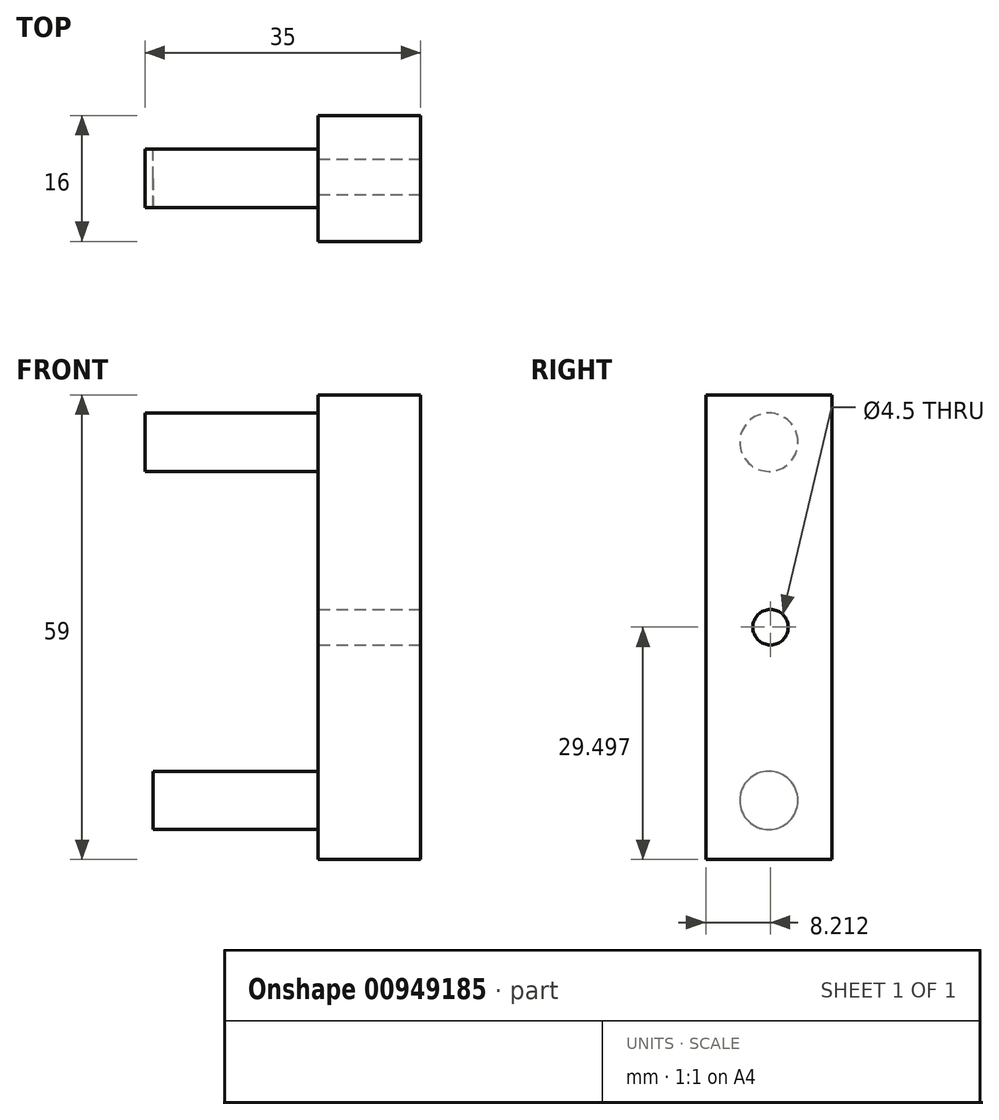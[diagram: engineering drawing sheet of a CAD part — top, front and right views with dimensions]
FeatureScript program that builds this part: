
annotation { "Feature Type Name" : "Feature", "Feature Type Description" : "" }
export const myFeature = defineFeature(function(context is Context, id is Id, definition is map)
    precondition{}
    {
        {
            var Q0;
            Q0=qCreatedBy(makeId("Front.planeOp"),FACE);
            var sketch = newSketch(context, id + "F0", { "sketchPlane" : qUnion([Q0])});
            skLineSegment(sketch, "E0.bottom", {"start": v(-12.8, 32) * mm, "end": v(0.2, 32) * mm});
            skLineSegment(sketch, "E1", {"start": v(-12.8, 32) * mm, "end": v(-12.8, 19.5) * mm});
            skLineSegment(sketch, "E2", {"start": v(-12.8, -8.5) * mm, "end": v(-12.8, -27) * mm});
            skLineSegment(sketch, "E3", {"start": v(0.2, 32) * mm, "end": v(0.2, -27) * mm});
            skLineSegment(sketch, "E4", {"start": v(0.2, -27) * mm, "end": v(-12.8, -27) * mm});
            skLineSegment(sketch, "E5", {"start": v(-12.8, 19.5) * mm, "end": v(-12.8, -8.5) * mm});
            skSolve(sketch);
        }
        {
            var Q0;
            Q0=makeQuery(id+"F0.imprint","IMPRINT",FACE,{"disambiguationData":[TD([[makeQuery(id+"F0.imprint","IMPRINT",EDGE,{"derivedFrom":sQuery(id+"F0.wireOp",EDGE,"E0.bottom")}),-1.0]])]});
            extrude(context, id + "F1", {"entities" : qUnion([Q0]), "depth" : 16 * mm, "offsetDistance" : 25 * mm});
        }
        {
            var Q0;
            Q0=makeQuery(id+"F1.opExtrude","SWEPT_FACE",FACE,{"disambiguationData":[OSD([sQuery(id+"F0.wireOp",EDGE,"E1")])]});
            var sketch = newSketch(context, id + "F2", { "sketchPlane" : qUnion([Q0])});
            skCircle(sketch, "E6", {"center": v(8, 26) * mm, "radius": 3.7 * mm});
            skCircle(sketch, "E7", {"center": v(8, -19.5) * mm, "radius": 3.7 * mm});
            skSolve(sketch);
        }
        {
            var Q0;
            Q0=makeQuery(id+"F2.imprint","IMPRINT",FACE,{"disambiguationData":[TD([[makeQuery(id+"F2.imprint","IMPRINT",EDGE,{"derivedFrom":sQuery(id+"F2.wireOp",EDGE,"E6")}),1.0]])]});
            extrude(context, id + "F3", {"entities" : qUnion([Q0]), "operationType" : NewBodyOperationType.ADD, "depth" : 22 * mm, "offsetDistance" : 25 * mm});
        }
        {
            var Q0;
            Q0=makeQuery(id+"F2.imprint","IMPRINT",FACE,{"disambiguationData":[TD([[makeQuery(id+"F2.imprint","IMPRINT",EDGE,{"derivedFrom":sQuery(id+"F2.wireOp",EDGE,"E7")}),1.0]])]});
            extrude(context, id + "F4", {"entities" : qUnion([Q0]), "operationType" : NewBodyOperationType.ADD, "depth" : 21 * mm, "offsetDistance" : 25 * mm});
        }
        {
            var Q0;
            Q0=makeQuery(id+"F1.opExtrude","SWEPT_FACE",FACE,{"disambiguationData":[OSD([sQuery(id+"F0.wireOp",EDGE,"E3")])]});
            var sketch = newSketch(context, id + "F5", { "sketchPlane" : qUnion([Q0])});
            skPoint(sketch, "E8", {"position": v(-7.79, 2.5) * mm});
            skSolve(sketch);
        }
        {
            var Q0;
            Q0=sQuery(id+"F5.wireOp",VERTEX,"E8");
            var Q1;
            Q1=makeQuery(id+"F1.opExtrude","SWEPT_BODY",BODY,{"disambiguationData":[OSD([sQuery(id+"F0.wireOp",EDGE,"E0.bottom"),sQuery(id+"F0.wireOp",EDGE,"E1"),sQuery(id+"F0.wireOp",EDGE,"E2"),sQuery(id+"F0.wireOp",EDGE,"E3"),sQuery(id+"F0.wireOp",EDGE,"E4"),sQuery(id+"F0.wireOp",EDGE,"E5")])]});
            hole(context, id + "F6", {"style" : HoleStyle.SIMPLE, "endStyle" : HoleEndStyle.THROUGH, "holeDiameter" : 4.5 * mm, "majorDiameter" : 5 * mm, "isTappedThrough" : true, "tappedDepth" : 12 * mm, "tapClearance" : 3, "locations" : qUnion([Q0]), "scope" : qUnion([Q1])});
        }
    });
